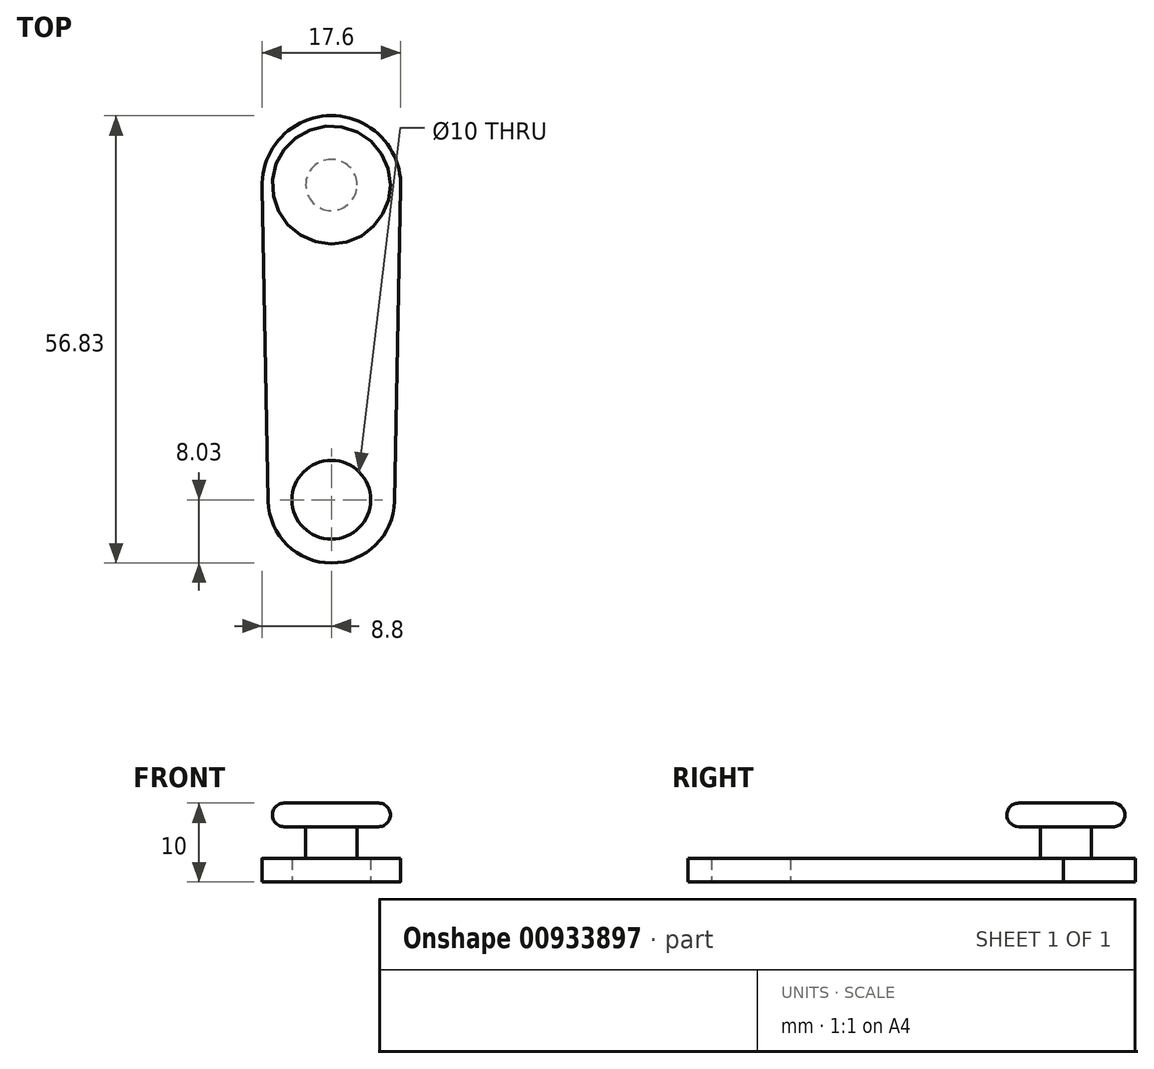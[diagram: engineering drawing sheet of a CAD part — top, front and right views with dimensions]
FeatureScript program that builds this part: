
annotation { "Feature Type Name" : "Feature", "Feature Type Description" : "" }
export const myFeature = defineFeature(function(context is Context, id is Id, definition is map)
    precondition{}
    {
        {
            var Q0;
            Q0=qCreatedBy(makeId("Top.planeOp"),FACE);
            var sketch = newSketch(context, id + "F0", { "sketchPlane" : qUnion([Q0])});
            skCircle(sketch, "E0", {"center": v(0, -40) * mm, "radius": 5 * mm});
            skArc(sketch, "E1", {"start": v(8.8, -0.34) * mm, "mid": v(0, 8.8) * mm, "end": v(-8.8, -0.34) * mm});
            skArc(sketch, "E2", {"start": v(-8.02, -40.16) * mm, "mid": v(0, -48.03) * mm, "end": v(8.02, -40.16) * mm});
            skLineSegment(sketch, "E3", {"start": v(-8.8, 0) * mm, "end": v(-8.02, -40.16) * mm});
            skLineSegment(sketch, "E4.MirrorCS", {"start": v(8.8, 0) * mm, "end": v(8.02, -40.16) * mm});
            skSolve(sketch);
        }
        {
            var Q0;
            Q0 = qSketchRegion(id + "F0", true);
            extrude(context, id + "F1", {"entities" : qUnion([Q0]), "depth" : 3 * mm, "offsetDistance" : 25 * mm});
        }
        {
            var Q0;
            Q0=makeQuery(id+"F1.opExtrude","CAP_FACE",FACE,{"disambiguationData":[OSD([sQuery(id+"F0.wireOp",EDGE,"E0"),sQuery(id+"F0.wireOp",EDGE,"E1"),sQuery(id+"F0.wireOp",EDGE,"E2"),sQuery(id+"F0.wireOp",EDGE,"E3"),sQuery(id+"F0.wireOp",EDGE,"E4.MirrorCS")])],"isStart":false});
            var sketch = newSketch(context, id + "F2", { "sketchPlane" : qUnion([Q0])});
            skCircle(sketch, "E5", {"center": v(0, 0) * mm, "radius": 3.25 * mm});
            skSolve(sketch);
        }
        {
            var Q0;
            Q0 = qSketchRegion(id + "F2", true);
            var Q1;
            Q1 = qConstructionFilter(qBodyType(qCreatedBy(id + "F2" ,EDGE), BodyType.WIRE), ConstructionObject.NO);
            extrude(context, id + "F3", {"entities" : qUnion([Q0]), "operationType" : NewBodyOperationType.ADD, "surfaceOperationType" : NewSurfaceOperationType.ADD, "surfaceEntities" : qUnion([Q1]), "depth" : 4 * mm, "offsetDistance" : 25 * mm});
        }
        {
            var Q0;
            Q0=makeQuery(id+"F3.opExtrude","CAP_FACE",FACE,{"disambiguationData":[OSD([sQuery(id+"F2.wireOp",EDGE,"E5")])],"isStart":false});
            var sketch = newSketch(context, id + "F4", { "sketchPlane" : qUnion([Q0])});
            skCircle(sketch, "E6", {"center": v(0, 0) * mm, "radius": 7.5 * mm});
            skSolve(sketch);
        }
        {
            var Q0;
            Q0 = qSketchRegion(id + "F4", true);
            extrude(context, id + "F5", {"entities" : qUnion([Q0]), "operationType" : NewBodyOperationType.ADD, "depth" : 3 * mm, "offsetDistance" : 25 * mm});
        }
        {
            var Q0;
            Q0=makeQuery(id+"F5.opExtrude","CAP_EDGE",EDGE,{"disambiguationData":[OSD([sQuery(id+"F4.wireOp",EDGE,"E6")])],"isStart":false});
            var Q1;
            Q1=makeQuery(id+"F5.opExtrude","CAP_EDGE",EDGE,{"disambiguationData":[OSD([sQuery(id+"F4.wireOp",EDGE,"E6")])],"isStart":true});
            fillet(context, id + "F6", {"entities" : qUnion([Q0, Q1]), "radius" : 1.5 * mm, "tangentPropagation" : true, "allowEdgeOverflow" : false});
        }
    });
